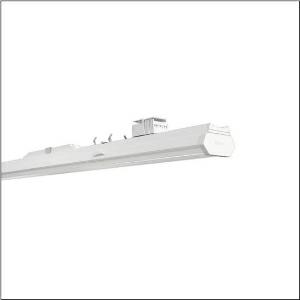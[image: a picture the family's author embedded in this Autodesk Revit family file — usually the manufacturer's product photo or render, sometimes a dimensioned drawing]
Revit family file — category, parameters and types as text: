
# Revit family: licross_11_protected_mo_51tp127n58xf
name_source: partatom
category: Lighting Fixtures
units: mm (PartAtom-declared; Revit-internal decimal feet)

## family parameters
Cut with Voids When Loaded = No
Host = Face
Light Source = No
Part Type = Normal
Room Calculation Point = No
Round Connector Dimension = Use Diameter
Shared = No

## types (1)
- Licross 11 Protected MO (1 x LED, 8120 lm, 47.6 W, 5000K)
    Apparent Load = 48 VA
    CIE Flux Codes = 73 92 98 99 100
    Color Rendering = 80
    Color Temperature = 5000K
    Default Elevation = 1800 mm
    Description = Licross 11 Protected MO, luminaire insert, of sheet steel, galvanised, coil coated, white, length: 1.500mm, width: 90mm, height: 101mm, LED rated luminous flux: 8.120lm, light colour: 850, SDCM (Standard Deviation of Colour Matching)MacAdam ≤ 3 SDCM (initial), control gear: ON/OFF, control gear: ECG, with plug, 3-pole, with phase selection, mains connection: 220..240V, AC, 50/60Hz, rated input power: 48W, internal wiring halogen-free, primary optical cover: cover, of PMMA, light emission: direct distribution, primary light characteristic: symmetric, protection rating (complete): IP64, insulation class (complete): insulation class I (protective earthing), certification: CE, ENEC, VDE, UKCA, protection symbol: D if used in an environment with conductive dust loads with corresponding accessories, impact resistance: IK06, permissible ambient temperature for indoor applications: -35..+45°C, reducing of maximum allowable ambient temperature of 5°C with ceiling mounting, corresponds to IFS (International Featured Standards) requirements for safety and quality in the food industry, LABS conformity tested according to VDMA 24364:2018-05, The light source and the operating device comply with the requirements of the Ecodesign Regulation (EU) 2019/2020 and are replaceable in accordance with this regulation, packaging unit: 1 piece
    Height = 92 mm
    Lamp = 1 x LED
    Lamp Light Flux = 8120 lm
    Lamp Power = 47.6 W
    Lamp count = 1
    Length = 1500 mm
    Luminous efficacy = 171 lm/W
    Manufacturer = Siteco
    ModVariant = No
    Model = 51TP127N58XF
    Mounting Place = Ceiling
    Mounting Type = Pendant
    Number of Poles = 1
    OnlyDefault = Yes
    Power Factor = 1
    Product Name = Licross 11 Protected MO
    Product group = luminaire insert | ceiling pendant
    ProductGroupID = 901
    Protection Class = Protection class I
    Protection Degree = IP 64
    RLX_Detail_Level = 1
    RLX_Emergency_Light_Flux = 0 lm
    RLX_Emergency_Type = 0
    RLX_Emergency_Type_DB = No
    RlxData = <blob elided: 20917 chars, md5=2996b82b>
    Socket = socket
    Standby Power = 0 W
    System Light Flux = 8120 lm
    System Power = 48 W
    Type Comments = Product without accessories
    Type Image = l_1256148.jpg
    URL = http://relux.com
    VarID = ---
    Voltage = 0 V
    Weight = 0.00 kg
    Width = 88 mm

## geometry (parser evidence)
native form markers: Blend x4, Sweep x11
no freeform markers — native parametric forms only
